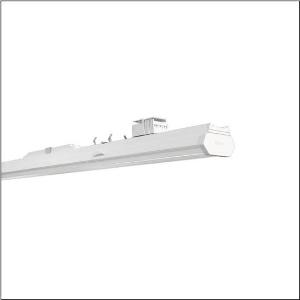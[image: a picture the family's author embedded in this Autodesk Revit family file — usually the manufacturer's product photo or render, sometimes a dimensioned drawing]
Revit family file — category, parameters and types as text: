
# Revit family: licross_r__21_protected_mo_52td12cn49xg_6de8
name_source: partatom
category: Lighting Fixtures
units: mm (PartAtom-declared; Revit-internal decimal feet)

## family parameters
Cut with Voids When Loaded = No
Host = Face
Light Source = No
Part Type = Normal
Room Calculation Point = No
Round Connector Dimension = Use Diameter
Shared = No

## types (1)
- --- (1 x LED, 9110 lm, 50.4 W, 4000K)
    Apparent Load = 50 VA
    CIE Flux Codes = 73 92 98 99 100
    Color Rendering = 80
    Color Temperature = 4000K
    Default Elevation = 1800 mm
    Description = Licross® 21 Protected MO, luminaire insert, of sheet steel, galvanised, coil coated, white, length: 1.500mm, width: 90mm, height: 103mm, LED rated luminous flux: 9.120lm, light colour: 840, control gear: ON/OFF Multilumen, CLOi, control gear: ECG Multilumen, with plug, 3-pole, with phase selection, mains connection: 220..240V, AC, 50/60Hz, start of lifetime: 50W, end of service life: 61W, halogen-free wiring, primary light control with lens, of plastic, primary optical cover: cover, of PMMA, light emission: direct distribution, primary light characteristic: symmetric, protection rating (complete): IP54, insulation class (complete): insulation class I (protective earthing), certification: CE, ENEC, VDE, UKCA, protection symbol: D if used in an environment with non-conductive dust loads with corresponding accessories, impact resistance: IK06, permissible ambient temperature for indoor applications: -35..+45°C, corresponds to IFS (International Featured Standards) requirements for safety and quality in the food industry, reducing of maximum allowable ambient temperature of 5°C with ceiling mounting, LABS conformity tested according to VDMA 24364:2018-05, packaging unit: 1 piece
    Height = 92 mm
    Lamp = 1 x LED
    Lamp Light Flux = 9110 lm
    Lamp Power = 50.4 W
    Lamp count = 1
    Length = 1500 mm
    Luminous efficacy = 181 lm/W
    Manufacturer = Siteco
    ModVariant = No
    Model = 52TD12CN49XG
    Mounting Place = Ceiling
    Mounting Type = Pendant
    Number of Poles = 1
    OnlyDefault = Yes
    Power Factor = 1
    Product Name = Licross® 21 Protected MO
    Product group = luminaire insert
    ProductGroupID = 901
    Protection Class = Protection class I
    Protection Degree = IP 54
    RLX_Detail_Level = 1
    RLX_Emergency_Light_Flux = 0 lm
    RLX_Emergency_Type = 0
    RLX_Emergency_Type_DB = No
    RlxData = <blob elided: 22261 chars, md5=077fa2b2>
    Socket = socket
    Standby Power = 0 W
    System Light Flux = 9110 lm
    System Power = 50 W
    Type Comments = factory setting: luminous flux: 100 % | (A | C | E) | 117 mA
    Type Image = l_1256148.jpg
    URL = http://relux.com
    VarID = @adj_080053
    Voltage = 0 V
    Weight = 0.00 kg
    Width = 88 mm

## geometry (parser evidence)
native form markers: Blend x4, Sweep x14
no freeform markers — native parametric forms only
